# Revit family: Electrical_Switchgear_Siemens_MV-Gas-insulated_NXPLUS-C-Wind-36kV
name_source: partatom
category: Electrical Fixtures
revit_build: Autodesk Revit 2016 (Build: 20161004_0715(x64)
units: mm (PartAtom-declared; Revit-internal decimal feet)

## family parameters
Always vertical = Yes
Cut with Voids When Loaded = No
Maintain Annotation Orientation = No
OmniClass Number = 23.80.00.00
OmniClass Title = Electric Power and Lighting
Part Type = Normal
Room Calculation Point = No
Round Connector Dimension = Use Diameter
Shared = No
Work Plane-Based = No

## types (3) — shared parameters
BIMobject category = Switchgear
BIMobject category code = electrical-switchgear
BIMobject main category = Electrical
BIMobject main category code = electrical
Brand url = https://www.siemens.com
Cabel_1 = Cabel : 1 cable
Cabel_2 = Cabel : 2  cable
Cabel_3 = Cabel : 3  cable
Cabel_without = Cabel : without
Capacitive voltage indicator at busbar = CAPDIS-S1+;CAPDIS-S2+;HR;LRM;VOIS+;VOIS R+;WEGA 1.2 C;WEGA 2.2 C
Consultant support for Totally Integrated Power (TIP) = www.siemens.com/tip-cs
Current transformer at busbar = without; with protection core or/and measuring core
Current transformer at feeder = without; with protection core or/and measuring core
Design country = Germany
Edition number = 1
Electromechanical interlock = without; Earthing switch; Disconnector; Disconnector and earthing switch
H = 1900 mm  [stored 6.2336 ft]
Installation instructions = https://www.siemens.com
Internal arc classification = IAC A FL 25kA/1s; IAC A FLR 25kA/1s
Manufacturer = Siemens AG
Manufacturer country = Germany
Manufacturer name = Siemens AG
Material main = Stainless steel
Nominal height = 1900 mm  [stored 6.2336 ft]
Pressure relief duct = withgout; on request: horizontal (connection to rear or lateral left or right)
Product Guid = 7b6fd002-bfc2-40cc-a29f-d81b13aac53f
Product SKU = Siemens_MV_switchgear_gas-insulated_NXPLUS_C_Wind
Product certification = https://www.siemens.com
Product data url = https://bimobject.com
Product family = MV switchgear
Product group = Gas-insulated switchgear for primary distribution systems
Product url = https://www.siemens.com
QR code = http://bimobject.com
Rated frequency (Hz) = 50;60
Rated lightning impulse withstand voltage (kV) = 170
Rated normal current busbar (A) = 1000
Rated short-duration power-frequency withstand voltage (kV) = 70
Rated short-time withstand current (kA/s) = 20/1:20/3; 25/1
Rated voltage (kV) = 36; on request: 38
SIMARIS planning tools = www.siemens.com/simaris
Specification texts = www.siemens.com/specifications
Standards = IEC
Surge arrester = without; with
Switchgear type = NXPLUS C Wind
T = 915 mm  [stored 3.00197 ft]
Technical description = http://www.siemens.com
Technical description MV-switchgear = www.siemens.com/medium-voltage-switchgear
Three-position switch = manual operated; motor operated
Type of arrangement = wall-standing; free-standing
Voltage rating (kV) = 2.4; 3.3; 3.6; 4.16; 4.76;6;6.6;7.2;8.25;11;12;13.8;15;17.5;20;23;24;27;27.6;34.5;36;38
Weight Net (Kg) = 0
Youtube clip = https://www.siemens.com
zero-valued in all types: Nominal width

## per-type parameters (varying)
| type | B | LinieLS | LinieRK | LinieTS | Model | Number of cables (per phase) | Number of operating cycle | Panel type | Protection device | Rated normal current feeder (A) | Release combination | Typ | Voltage transformer at busbar |
| LS-Circuit-breaker panel | 600 mm  [stored 1.9685 ft] | Yes | No | No | LS-Circuit-breaker panel, width 600mm | 1; 2 | 2000/1000/1000 (CB/Disconnector/Earthing switch) | LS | with (further informations: www.siemens.com/protection) | 630A; 800A | 1f-release (-Y1); 1f- (-Y1) + 1r-release (-Y7); 2f-release (-Y1, -Y2) | 1 | without; 3 x single-pole; 3 x single-pole with earth-fault winding and damping resistor |
| RK-Ring-main panel | 450 mm  [stored 1.47638 ft] | No | Yes | No | RK-Ring-main panel, width 450mm | 1; 2; 3 | 1000/1000/1000 (Disconnector/Load Break/Earthing switch) | RK |  | 630A |  | 2 |  |
| TS-Disconnector panel | 450 mm  [stored 1.47638 ft] | No | No | Yes | TS-Disconnector panel, width 450mm | 1; 2; 3 | 1000/1000/- (Disconnector/Earthing switch) | TS |  | 630A; 1000A |  | 3 |  |

note: [stored X ft] marks values corroborated as IEEE doubles in the binary element streams (Revit-internal decimal feet)

## geometry (parser evidence)
native form markers: Blend x2, Sweep x8
no freeform markers — native parametric forms only
